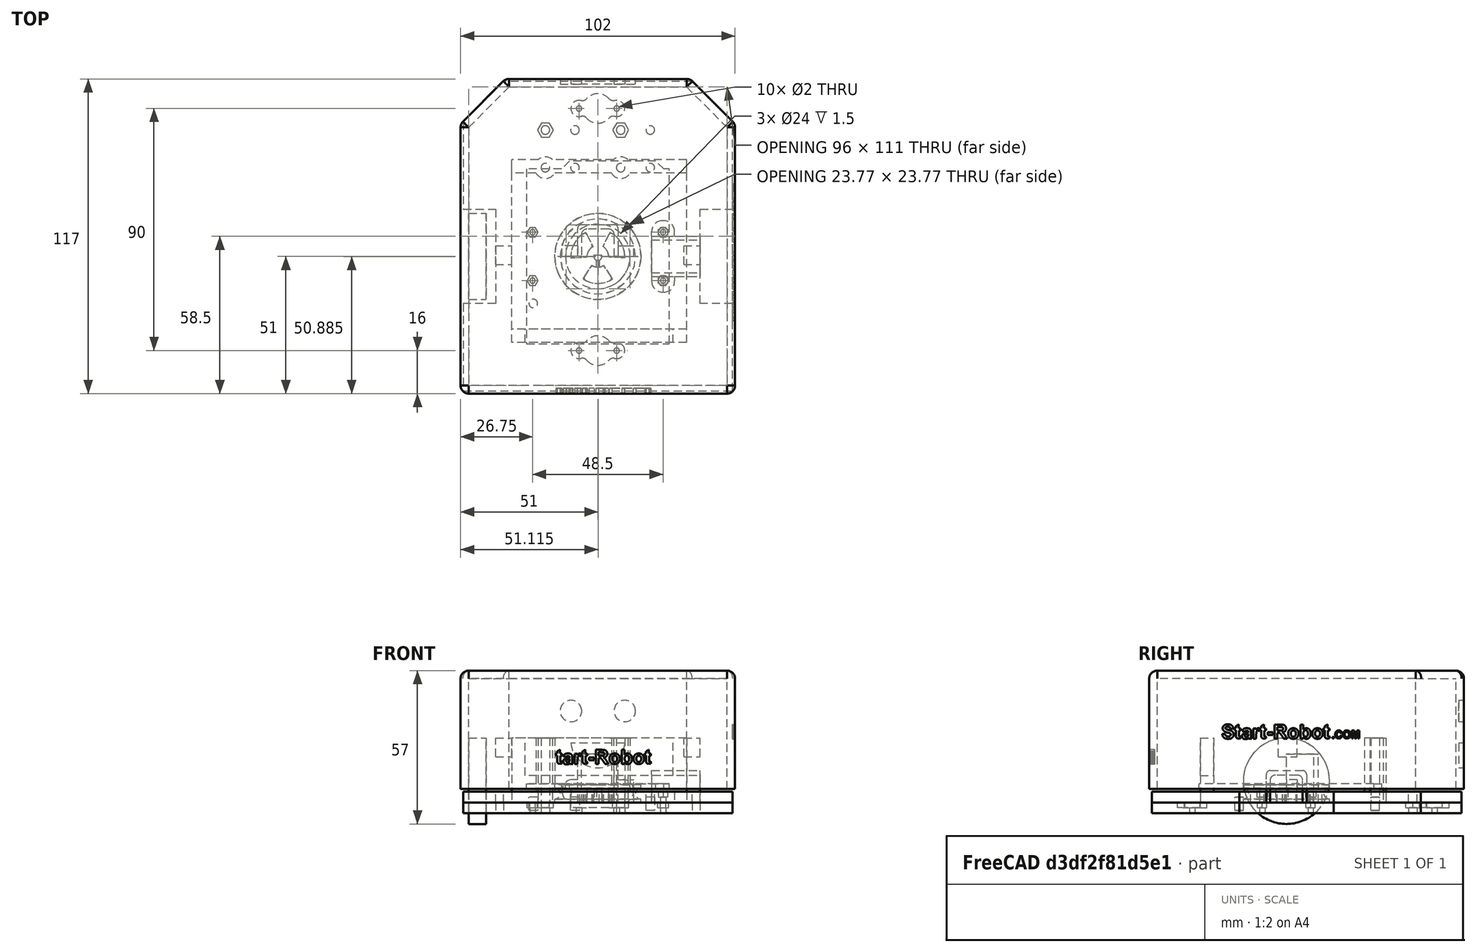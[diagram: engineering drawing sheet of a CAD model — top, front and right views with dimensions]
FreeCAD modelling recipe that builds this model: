
FCSTD DOCUMENT  (FreeCAD 0.14R3700 (Git))
Label: piezasStartCar
License: CC-BY 3.0
LicenseURL: http://creativecommons.org/licenses/by/3.0/
objects: Part::Cut×37, Part::Cylinder×23, Part::Extrusion×16, Part::Feature×15, Sketcher::SketchObject×13, Part::Prism×8, PartDesign::Pocket×7, PartDesign::Pad×6, Part::Box×6, Part::MultiFuse×4, PartDesign::Fillet×3, Mesh::Feature×1, Part::Thickness×1, Part::Torus×1, PartDesign::PolarPattern×1, Part::Fillet×1
note: 155 computed .brp shape members not serialized (recipe doc carries the construction recipe); baked Part::Feature solids carry a one-line shape summary decoded from their .brp

FEATURE [Sketcher::SketchObject] Sketch
  sketch-geometry (14):
    g0: LineSegment StartX=-35 StartY=65 StartZ=0 EndX=35 EndY=65 EndZ=0
    g1: LineSegment StartX=35 StartY=65 StartZ=0 EndX=50 EndY=50 EndZ=0
    g2: LineSegment StartX=50 StartY=50 StartZ=0 EndX=50 EndY=17.5 EndZ=0
    g3: LineSegment StartX=50 StartY=17.5 StartZ=0 EndX=38 EndY=17.5 EndZ=0
    g4: LineSegment StartX=38 StartY=17.5 StartZ=0 EndX=38 EndY=-17.5 EndZ=0
    g5: LineSegment StartX=38 StartY=-17.5 StartZ=0 EndX=50 EndY=-17.5 EndZ=0
    g6: LineSegment StartX=50 StartY=-17.5 StartZ=0 EndX=50 EndY=-50 EndZ=0
    g7: LineSegment StartX=50 StartY=-50 StartZ=0 EndX=-50 EndY=-50 EndZ=0
    g8: LineSegment StartX=-50 StartY=-50 StartZ=0 EndX=-50 EndY=-17.5 EndZ=0
    g9: LineSegment StartX=-50 StartY=-17.5 StartZ=0 EndX=-38 EndY=-17.5 EndZ=0
    g10: LineSegment StartX=-38 StartY=-17.5 StartZ=0 EndX=-38 EndY=17.5 EndZ=0
    g11: LineSegment StartX=-38 StartY=17.5 StartZ=0 EndX=-50 EndY=17.5 EndZ=0
    g12: LineSegment StartX=-50 StartY=17.5 StartZ=0 EndX=-50 EndY=50 EndZ=0
    g13: LineSegment StartX=-50 StartY=50 StartZ=0 EndX=-35 EndY=65 EndZ=0
  constraints (42):
    c: Horizontal(g0)
    c: Coincident(g0,g1)
    c: Coincident(g1,g2)
    c: Vertical(g2)
    c: Coincident(g2,g3)
    c: Coincident(g3,g4)
    c: Coincident(g4,g5)
    c: Coincident(g5,g6)
    c: Vertical(g6)
    c: Coincident(g6,g7)
    c: Horizontal(g7)
    c: Coincident(g7,g8)
    c: Vertical(g8)
    c: Coincident(g8,g9)
    c: Horizontal(g9)
    c: Coincident(g9,g10)
    c: Vertical(g10)
    c: Coincident(g10,g11)
    c: Horizontal(g11)
    c: Coincident(g11,g12)
    c: Coincident(g12,g13)
    c: Coincident(g13,g0)
    c: Equal(g12,g2)
    c: Vertical(g12)
    c: Equal(g10,g4)
    c: Vertical(g4)
    c: Equal(g6,g8)
    c: Equal(g11,g9)
    c: Equal(g3,g5)
    c: Horizontal(g3)
    c: Horizontal(g5)
    c: Symmetric(g0,g0,g-2)
    c: Symmetric(g6,g7,g-2)
    c: DistanceX(g7) = -100
    c: DistanceX(g3) = -12
    c: DistanceX(g11) = -12
    c: DistanceY(g10) = 35
    c: DistanceY(g6) = -32.5
    c: DistanceY(g2) = -32.5
    c: DistanceX(g0) = 70
    c: Angle(g12,g13) = 2.35619
    c: Symmetric(g3,g4,g-1)
FEATURE [PartDesign::Pad] Pad  label="Base"
  Length = 4
  Length2 = 100
  Sketch = -> Sketch
  Type = 0
FEATURE [Sketcher::SketchObject] Sketch001
  Placement = pos=(0,0,5) rot=(0,0,1;0rad)
  sketch-geometry (9):
    g0: LineSegment StartX=-26.5 StartY=32.5 StartZ=0 EndX=-26.5 EndY=-32.5 EndZ=0
    g1: LineSegment StartX=-26.5 StartY=-32.5 StartZ=0 EndX=26.5 EndY=-32.5 EndZ=0
    g2: LineSegment StartX=26.5 StartY=-32.5 StartZ=0 EndX=26.5 EndY=32.5 EndZ=0
    g3: LineSegment StartX=26.5 StartY=32.5 StartZ=0 EndX=24.5 EndY=32.5 EndZ=0
    g4: LineSegment StartX=24.5 StartY=32.5 StartZ=0 EndX=21.5 EndY=35.5 EndZ=0
    g5: LineSegment StartX=21.5 StartY=35.5 StartZ=0 EndX=-10.5 EndY=35.5 EndZ=0
    g6: LineSegment StartX=-10.5 StartY=35.5 StartZ=0 EndX=-13.5 EndY=32.5 EndZ=0
    g7: LineSegment StartX=-13.5 StartY=32.5 StartZ=0 EndX=-26.5 EndY=32.5 EndZ=0
    g8: LineSegment [constr] StartX=-10.5 StartY=35.5 StartZ=0 EndX=-10.5 EndY=-32.5 EndZ=0
  constraints (27):
    c: Vertical(g0)
    c: Coincident(g0,g1)
    c: Horizontal(g1)
    c: Coincident(g1,g2)
    c: Vertical(g2)
    c: Coincident(g2,g3)
    c: Coincident(g3,g4)
    c: Coincident(g4,g5)
    c: Horizontal(g5)
    c: Coincident(g5,g6)
    c: Coincident(g6,g7)
    c: Coincident(g7,g0)
    c: Horizontal(g7)
    c: Equal(g0,g2)
    c: DistanceY(g2) = 65
    c: Coincident(g8,g5)
    c: PointOnObject(g8,g1)
    c: Vertical(g8)
    c: DistanceY(g8) = -68
    c: Horizontal(g3)
    c: DistanceX(g1) = 53
    c: DistanceX(g5) = -32
    c: DistanceX(g3) = -2
    c: DistanceX(g7) = -13
    c: Angle(g6,g5) = 2.35619
    c: Symmetric(g0,g1,g-2)
    c: Symmetric(g0,g0,g-1)
FEATURE [PartDesign::Pad] Pad001
  Length = 2
  Length2 = 100
  Placement = pos=(0,0,5) rot=(0,0,1;0rad)
  Sketch = -> Sketch001
  Type = 0
FEATURE [Sketcher::SketchObject] Sketch002
  ExternalGeometry = -> [Pad001]
  Placement = pos=(0,0,7) rot=(0,0,1;0rad)
  Support = -> Pad001 [Face10]
  sketch-geometry (3):
    g0: Circle CenterX=-24 CenterY=-17.5 CenterZ=0 NormalX=0 NormalY=0 NormalZ=1 Radius=1.6
    g1: Circle CenterX=-8.5 CenterY=33 CenterZ=0 NormalX=0 NormalY=0 NormalZ=1 Radius=1.6
    g2: Circle CenterX=19.5 CenterY=33 CenterZ=0 NormalX=0 NormalY=0 NormalZ=1 Radius=1.6
  constraints (9):
    c: Radius(g0) = 1.6
    c: DistanceY(g0,g-3) = -15
    c: DistanceX(g0,g-3) = 50.5
    c: Equal(g1,g2)
    c: Equal(g2,g0)
    c: DistanceX(g1,g-4) = 35
    c: DistanceY(g1,g-4) = -65.5
    c: DistanceY(g2,g-4) = -65.5
    c: DistanceX(g2,g-4) = 7
FEATURE [PartDesign::Pocket] Pocket  label="Arduino"
  Length = 5
  Placement = pos=(0,0,5) rot=(0,0,1;0rad)
  Sketch = -> Sketch002
  Type = 0
FEATURE [Sketcher::SketchObject] Sketch003
  sketch-geometry (12):
    g0: LineSegment StartX=-6.075 StartY=0 StartZ=0 EndX=-7.5 EndY=0 EndZ=0
    g1: LineSegment StartX=-7.5 StartY=0 StartZ=0 EndX=-7.5 EndY=10.3588 EndZ=0
    g2: LineSegment StartX=-6 StartY=11.8588 StartZ=0 EndX=6 EndY=11.8588 EndZ=0
    g3: LineSegment StartX=7.5 StartY=10.3588 StartZ=0 EndX=7.5 EndY=0 EndZ=0
    g4: LineSegment StartX=7.5 StartY=0 StartZ=0 EndX=6.075 EndY=0 EndZ=0
    g5: LineSegment StartX=6.075 StartY=0 StartZ=0 EndX=6.075 EndY=8.15 EndZ=0
    g6: LineSegment StartX=4.075 StartY=10.15 StartZ=0 EndX=-4.075 EndY=10.15 EndZ=0
    g7: LineSegment StartX=-6.075 StartY=8.15 StartZ=0 EndX=-6.075 EndY=0 EndZ=0
    g8: ArcOfCircle CenterX=6 CenterY=10.3588 CenterZ=0 NormalX=0 NormalY=0 NormalZ=1 Radius=1.5 StartAngle=0 EndAngle=1.5708
    g9: ArcOfCircle CenterX=-6 CenterY=10.3588 CenterZ=0 NormalX=0 NormalY=0 NormalZ=1 Radius=1.5 StartAngle=1.5708 EndAngle=3.14159
    g10: ArcOfCircle CenterX=4.075 CenterY=8.15 CenterZ=0 NormalX=0 NormalY=0 NormalZ=1 Radius=2 StartAngle=0 EndAngle=1.5708
    g11: ArcOfCircle CenterX=-4.075 CenterY=8.15 CenterZ=0 NormalX=0 NormalY=0 NormalZ=1 Radius=2 StartAngle=1.5708 EndAngle=3.14159
  constraints (31):
    c: Horizontal(g0)
    c: Coincident(g0,g1)
    c: Vertical(g1)
    c: Horizontal(g2)
    c: PointOnObject(g3,g-1)
    c: Vertical(g3)
    c: Coincident(g3,g4)
    c: Coincident(g4,g5)
    c: Vertical(g5)
    c: Horizontal(g6)
    c: Coincident(g7,g0)
    c: Vertical(g7)
    c: Horizontal(g4)
    c: Equal(g0,g4)
    c: DistanceX(g0,g3) = 15
    c: DistanceX(g0,g4) = 12.15
    c: Tangent(g2,g8)
    c: Tangent(g3,g8)
    c: Tangent(g2,g9)
    c: Tangent(g1,g9)
    c: Radius(g9) = 1.5
    c: Radius(g8) = 1.5
    c: Tangent(g6,g10)
    c: Tangent(g5,g10)
    c: Tangent(g6,g11)
    c: Tangent(g7,g11)
    c: Radius(g10) = 2
    c: Radius(g11) = 2
    c: DistanceY(g6,g0) = -10.15
    c: DistanceY(g4,g6) = 10.15
    c: Symmetric(g0,g3,g-2)
FEATURE [PartDesign::Pad] Pad002
  Length = 18
  Length2 = 100
  Sketch = -> Sketch003
  Type = 0
FEATURE [Sketcher::SketchObject] Sketch004
  Placement = pos=(7.5,0,0) rot=(0.57735,0.57735,0.57735;2.0944rad)
  Support = -> Pad002 [Face1]
  sketch-geometry (4):
    g0: LineSegment StartX=0 StartY=0 StartZ=0 EndX=4 EndY=0 EndZ=0
    g1: LineSegment StartX=4 StartY=0 StartZ=0 EndX=4 EndY=8.5 EndZ=0
    g2: LineSegment StartX=4 StartY=8.5 StartZ=0 EndX=0 EndY=8.5 EndZ=0
    g3: LineSegment StartX=0 StartY=8.5 StartZ=0 EndX=0 EndY=0 EndZ=0
  constraints (11):
    c: Coincident(g0,g1)
    c: Coincident(g1,g2)
    c: Coincident(g2,g3)
    c: Coincident(g3,g0)
    c: Horizontal(g0)
    c: Horizontal(g2)
    c: Vertical(g1)
    c: Vertical(g3)
    c: Coincident(g0,g-1)
    c: DistanceY(g1) = 8.5
    c: DistanceX(g2) = -4
FEATURE [PartDesign::Pad] Pad003
  Length = 5.8
  Length2 = 100
  Sketch = -> Sketch004
  Type = 0
FEATURE [Sketcher::SketchObject] Sketch005
  Placement = pos=(-7.5,0,0) rot=(0.57735,-0.57735,-0.57735;2.0944rad)
  Support = -> Pad003 [Face10]
  sketch-geometry (4):
    g0: LineSegment StartX=0 StartY=0 StartZ=0 EndX=-4 EndY=0 EndZ=0
    g1: LineSegment StartX=-4 StartY=0 StartZ=0 EndX=-4 EndY=8.5 EndZ=0
    g2: LineSegment StartX=-4 StartY=8.5 StartZ=0 EndX=0 EndY=8.5 EndZ=0
    g3: LineSegment StartX=0 StartY=8.5 StartZ=0 EndX=0 EndY=0 EndZ=0
  constraints (11):
    c: Coincident(g0,g1)
    c: Coincident(g1,g2)
    c: Coincident(g2,g3)
    c: Coincident(g3,g0)
    c: Horizontal(g0)
    c: Horizontal(g2)
    c: Vertical(g1)
    c: Vertical(g3)
    c: Coincident(g0,g-1)
    c: DistanceX(g2) = 4
    c: DistanceY(g1) = 8.5
FEATURE [Part::Prism] Prism  label="Prisma"
  Circumradius = 2
  Height = 2
  Placement = pos=(-9,4,4.25) rot=(1,0,0;1.5708rad)
  Polygon = 6
FEATURE [Part::Prism] Prism002  label="Prisma002"
  Circumradius = 2
  Height = 2
  Placement = pos=(9,4,4.25) rot=(1,0,0;1.5708rad)
  Polygon = 6
FEATURE [Part::Box] Box  label="CNY70"
  Height = 7
  Length = 6
  Placement = pos=(-38,-3,17) rot=(0,0,1;0rad)
  Width = 7
FEATURE [Part::Box] Box001  label="CNY071"
  Height = 7
  Length = 6
  Placement = pos=(32,-3,17) rot=(0,0,1;0rad)
  Width = 7
FEATURE [Part::Cylinder] Cylinder  label="Rueda1"
  Angle = 360
  Height = 6.5
  Radius = 16
FEATURE [Part::Cylinder] Cylinder001  label="Rueda2"
  Angle = 360
  Height = 6.5
  Placement = pos=(-48,0,8) rot=(0,1,0;1.5708rad)
  Radius = 16
FEATURE [Mesh::Feature] baseArduino
  Placement = pos=(0,14,24) rot=(0,0,1;0rad)
FEATURE [Part::Box] Box002  label="Cubo"
  Height = 24
  Length = 65
  Placement = pos=(-33,-18,5) rot=(0,0,1;0rad)
  Width = 5
FEATURE [Part::Box] Box003  label="Cubo001"
  Height = 4
  Length = 65
  Placement = pos=(-33,-13,25) rot=(0,0,1;0rad)
  Width = 63
FEATURE [Part::Box] Box004  label="Cubo002"
  Height = 20
  Length = 65
  Placement = pos=(-33,45,5) rot=(0,0,1;0rad)
  Width = 5
FEATURE [Part::Cylinder] Cylinder003  label="Cilindro001"
  Angle = 360
  Height = 24
  Placement = pos=(19.5,47,5) rot=(0,0,1;0rad)
  Radius = 4
FEATURE [Part::Box] Box005  label="Cubo003"
  Height = 16
  Length = 55
  Placement = pos=(-28,-21,3) rot=(0,0,1;0rad)
  Width = 9
FEATURE [Part::Cylinder] Cylinder004  label="Cilindro002"
  Angle = 360
  Height = 37
  Placement = pos=(-8.5,47,-2) rot=(0,0,1;0rad)
  Radius = 1.6
FEATURE [Part::Cylinder] Cylinder005  label="Cilindro003"
  Angle = 360
  Height = 37
  Placement = pos=(19.5,47,-2) rot=(0,0,1;0rad)
  Radius = 1.6
FEATURE [Part::Cut] Cut006
  Base = -> Pad
  Tool = -> Cylinder004
FEATURE [Part::Cut] Cut008  label="Base001"
  Base = -> Cut006
  Tool = -> Cylinder005
FEATURE [Sketcher::SketchObject] Sketch010
  Placement = pos=(0,0,5) rot=(0,0,1;0rad)
  sketch-geometry (6):
    g0: LineSegment StartX=-33 StartY=63 StartZ=0 EndX=33 EndY=63 EndZ=0
    g1: LineSegment StartX=33 StartY=63 StartZ=0 EndX=48 EndY=48 EndZ=0
    g2: LineSegment StartX=48 StartY=-48 StartZ=0 EndX=-48 EndY=-48 EndZ=0
    g3: LineSegment StartX=-48 StartY=48 StartZ=0 EndX=-33 EndY=63 EndZ=0
    g4: LineSegment StartX=-48 StartY=48 StartZ=0 EndX=-48 EndY=-48 EndZ=0
    g5: LineSegment StartX=48 StartY=48 StartZ=0 EndX=48 EndY=-48 EndZ=0
  constraints (18):
    c: Horizontal(g0)
    c: Coincident(g0,g1)
    c: Horizontal(g2)
    c: Coincident(g3,g0)
    c: Symmetric(g0,g0,g-2)
    c: DistanceX(g2) = -96
    c: DistanceX(g0) = 66
    c: Coincident(g4,g3)
    c: Coincident(g4,g2)
    c: Vertical(g4)
    c: Coincident(g5,g1)
    c: Coincident(g5,g2)
    c: Vertical(g5)
    c: Equal(g5,g4)
    c: DistanceY(g5) = -96
    c: Symmetric(g1,g2,g-1)
    c: Angle(g4,g3) = 2.35619
    c: Angle(g1,g5) = 2.35619
FEATURE [PartDesign::Pad] Pad008  label="Base005"
  Length = 41
  Length2 = 100
  Placement = pos=(0,0,5) rot=(0,0,1;0rad)
  Sketch = -> Sketch010
  Type = 0
FEATURE [Part::Feature] path001
  shape: bbox 2.248 x 5.23 x 2e-07 mm, 0 faces, 0 solids (baked)
FEATURE [Part::Feature] path002
  shape: bbox 3.533 x 4.091 x 2e-07 mm, 0 faces, 0 solids (baked)
FEATURE [Part::Feature] path003
  shape: bbox 1.357 x 1.203 x 2e-07 mm, 0 faces, 0 solids (baked)
FEATURE [Part::Feature] path004
  shape: bbox 2.463 x 3.887 x 2e-07 mm, 0 faces, 0 solids (baked)
FEATURE [Part::Feature] path005
  shape: bbox 2.248 x 5.23 x 2e-07 mm, 0 faces, 0 solids (baked)
FEATURE [Part::Feature] path006
  shape: bbox 1.976 x 1.006 x 2e-07 mm, 0 faces, 0 solids (baked)
FEATURE [Part::Feature] path007
  shape: bbox 4.718 x 5.247 x 2e-07 mm, 0 faces, 0 solids (baked)
FEATURE [Part::Feature] path008
  shape: bbox 2.14 x 1.332 x 2e-07 mm, 0 faces, 0 solids (baked)
FEATURE [Part::Feature] path009
  shape: bbox 3.923 x 3.973 x 2e-07 mm, 0 faces, 0 solids (baked)
FEATURE [Part::Feature] path010
  shape: bbox 1.858 x 2.334 x 2e-07 mm, 0 faces, 0 solids (baked)
FEATURE [Part::Feature] path011
  shape: bbox 3.712 x 5.333 x 2e-07 mm, 0 faces, 0 solids (baked)
FEATURE [Part::Feature] path012
  shape: bbox 1.682 x 2.409 x 2e-07 mm, 0 faces, 0 solids (baked)
FEATURE [Part::Feature] path013
  shape: bbox 3.923 x 3.973 x 2e-07 mm, 0 faces, 0 solids (baked)
FEATURE [Part::Feature] path014
  shape: bbox 1.858 x 2.334 x 2e-07 mm, 0 faces, 0 solids (baked)
FEATURE [Part::Feature] path015
  shape: bbox 2.248 x 5.23 x 2e-07 mm, 0 faces, 0 solids (baked)
FEATURE [Part::Extrusion] Extrude001
  Base = -> path001
  Dir = (0,0,2)
  Solid = true
FEATURE [Part::Extrusion] Extrude002
  Base = -> path002
  Dir = (0,0,2)
  Solid = true
FEATURE [Part::Extrusion] Extrude003
  Base = -> path003
  Dir = (0,0,2)
  Solid = true
FEATURE [Part::Extrusion] Extrude004
  Base = -> path004
  Dir = (0,0,2)
  Solid = true
FEATURE [Part::Extrusion] Extrude005
  Base = -> path005
  Dir = (0,0,2)
  Solid = true
FEATURE [Part::Extrusion] Extrude006
  Base = -> path006
  Dir = (0,0,2)
  Solid = true
FEATURE [Part::Extrusion] Extrude007
  Base = -> path007
  Dir = (0,0,2)
  Solid = true
FEATURE [Part::Extrusion] Extrude008
  Base = -> path008
  Dir = (0,0,2)
  Solid = true
FEATURE [Part::Extrusion] Extrude009
  Base = -> path009
  Dir = (0,0,2)
  Solid = true
FEATURE [Part::Extrusion] Extrude010
  Base = -> path010
  Dir = (0,0,2)
  Solid = true
FEATURE [Part::Extrusion] Extrude011
  Base = -> path011
  Dir = (0,0,2)
  Solid = true
FEATURE [Part::Extrusion] Extrude012
  Base = -> path012
  Dir = (0,0,2)
  Solid = true
FEATURE [Part::Extrusion] Extrude013
  Base = -> path013
  Dir = (0,0,2)
  Solid = true
FEATURE [Part::Extrusion] Extrude014
  Base = -> path014
  Dir = (0,0,2)
  Solid = true
FEATURE [Part::Extrusion] Extrude015
  Base = -> path015
  Dir = (0,0,2)
  Solid = true
FEATURE [Part::Cut] Cut011
  Base = -> Extrude002
  Tool = -> Extrude003
FEATURE [Part::Cut] Cut012
  Base = -> Extrude007
  Tool = -> Extrude008
FEATURE [Part::Cut] Cut013
  Base = -> Extrude009
  Tool = -> Extrude010
FEATURE [Part::Cut] Cut014
  Base = -> Extrude011
  Tool = -> Extrude012
FEATURE [Part::Cut] Cut015
  Base = -> Extrude013
  Tool = -> Extrude014
FEATURE [Part::MultiFuse] Fusion002  label="Nombre"
  Placement = pos=(-3,-49,20) rot=(1,0,0;1.5708rad)
  Shapes = -> [Cut014,Extrude001,Extrude004,Extrude005,Extrude006,Extrude015,Cut015,Cut013,Cut011,Cut012]
FEATURE [Part::Thickness] Thickness
  Faces = -> Pad008 [Face7]
  Intersection = false
  Join = 0
  Mode = 0
  SelfIntersection = false
  Value = 3
FEATURE [Sketcher::SketchObject] Sketch011
  Placement = pos=(0,0,4) rot=(0,0,1;0rad)
  Support = -> Cut008 [Face5]
  sketch-geometry (4):
    g0: Circle CenterX=-7 CenterY=55 CenterZ=0 NormalX=0 NormalY=0 NormalZ=1 Radius=1
    g1: Circle CenterX=7 CenterY=55 CenterZ=0 NormalX=0 NormalY=0 NormalZ=1 Radius=1
    g2: Circle CenterX=-7 CenterY=-35 CenterZ=0 NormalX=0 NormalY=0 NormalZ=1 Radius=1
    g3: Circle CenterX=7 CenterY=-35 CenterZ=0 NormalX=0 NormalY=0 NormalZ=1 Radius=1
  constraints (10):
    c: Equal(g0,g1)
    c: Equal(g1,g3)
    c: Equal(g3,g2)
    c: Radius(g0) = 1
    c: DistanceX(g2,g3) = 14
    c: Symmetric(g3,g2,g-2)
    c: DistanceX(g1,g0) = -14
    c: Symmetric(g1,g0,g-2)
    c: DistanceY(g-1,g1) = 55
    c: DistanceY(g-1,g2) = -35
FEATURE [PartDesign::Pocket] Pocket002  label="BaseCoche"
  Length = 5
  Sketch = -> Sketch011
  Type = 0
FEATURE [Part::Cylinder] Cylinder009  label="Cilindro007"
  Angle = 360
  Height = 11
  Placement = pos=(-24.25,9,-3) rot=(0,0,1;0rad)
  Radius = 1
FEATURE [Part::Cylinder] Cylinder010  label="Cilindro008"
  Angle = 360
  Height = 11
  Placement = pos=(-24.25,-9,-3) rot=(0,0,1;0rad)
  Radius = 1
FEATURE [Part::Cylinder] Cylinder011  label="Cilindro009"
  Angle = 360
  Height = 11
  Placement = pos=(24.25,-9,-2) rot=(0,0,1;0rad)
  Radius = 1
FEATURE [Part::Cylinder] Cylinder012  label="Cilindro010"
  Angle = 360
  Height = 11
  Placement = pos=(24.25,9,-3) rot=(0,0,1;0rad)
  Radius = 1
FEATURE [Part::Cut] Cut016
  Base = -> Pocket002
  Tool = -> Cylinder009
FEATURE [Part::Cut] Cut017
  Base = -> Cut016
  Tool = -> Cylinder010
FEATURE [Part::Cut] Cut018
  Base = -> Cut017
  Tool = -> Cylinder011
FEATURE [Part::Cut] Cut019
  Base = -> Cut018
  Placement = pos=(0,0,0) rot=(0,1,0;3.14159rad)
  Tool = -> Cylinder012
FEATURE [Part::Cylinder] Cylinder013  label="Cilindro011"
  Angle = 360
  Height = 24
  Placement = pos=(-8.5,47,5) rot=(0,0,1;0rad)
  Radius = 4
FEATURE [Part::MultiFuse] Fusion
  Shapes = -> [Box002,Box003,Box004,Cylinder003,Cylinder013]
FEATURE [Part::Cut] Cut004
  Base = -> Fusion
  Tool = -> Box005
FEATURE [Part::Cut] Cut005
  Base = -> Cut004
  Tool = -> Cylinder004
FEATURE [Part::Prism] Prism003  label="Prisma003"
  Circumradius = 2
  Height = 4
  Polygon = 6
FEATURE [Part::Cylinder] Cylinder014  label="Cilindro"
  Angle = 360
  Height = 10
  Placement = pos=(0,0,-3) rot=(0,0,1;0rad)
  Radius = 1
FEATURE [Part::Cut] Cut020
  Base = -> Prism003
  Placement = pos=(-24.25,9,-2) rot=(0,0,1;0rad)
  Tool = -> Cylinder014
FEATURE [Part::Cylinder] Cylinder015  label="Cilindro012"
  Angle = 360
  Height = 10
  Placement = pos=(0,0,-3) rot=(0,0,1;0rad)
  Radius = 1
FEATURE [Part::Prism] Prism004  label="Prisma004"
  Circumradius = 2
  Height = 2
  Polygon = 6
FEATURE [Part::Cut] Cut021
  Base = -> Prism004
  Placement = pos=(-24.25,-9,-2) rot=(0,0,1;0rad)
  Tool = -> Cylinder015
FEATURE [Part::Cylinder] Cylinder016  label="Cilindro013"
  Angle = 360
  Height = 10
  Placement = pos=(0,0,-3) rot=(0,0,1;0rad)
  Radius = 1
FEATURE [Part::Prism] Prism005  label="Prisma005"
  Circumradius = 2
  Height = 2
  Polygon = 6
FEATURE [Part::Cut] Cut022
  Base = -> Prism005
  Placement = pos=(24.25,9,-2) rot=(0,0,1;0rad)
  Tool = -> Cylinder016
FEATURE [Part::Cylinder] Cylinder017  label="Cilindro014"
  Angle = 360
  Height = 10
  Placement = pos=(0,0,-3) rot=(0,0,1;0rad)
  Radius = 1
FEATURE [Part::Prism] Prism006  label="Prisma006"
  Circumradius = 2
  Height = 2
  Polygon = 6
FEATURE [Part::Cut] Cut023
  Base = -> Prism006
  Placement = pos=(24.25,-9,-2) rot=(0,0,1;0rad)
  Tool = -> Cylinder017
FEATURE [Part::Cut] Cut024
  Base = -> Cut019
  Tool = -> Cut020
FEATURE [Part::Cut] Cut025
  Base = -> Cut024
  Tool = -> Cut023
FEATURE [Part::Cut] Cut026
  Base = -> Cut025
  Tool = -> Cut022
FEATURE [Part::Cut] Cut027
  Base = -> Cut026
  Tool = -> Cut021
FEATURE [Part::Prism] Prism007  label="Prisma007"
  Circumradius = 3
  Height = 2
  Polygon = 6
FEATURE [Part::Cylinder] Cylinder018  label="Cilindro015"
  Angle = 360
  Height = 10
  Radius = 1.5
FEATURE [Part::Cut] Cut028  label="primas3M01"
  Base = -> Prism007
  Placement = pos=(-19.5,47,-2) rot=(0,0,1;0rad)
  Tool = -> Cylinder018
FEATURE [Part::Prism] Prism008  label="Prisma008"
  Circumradius = 3
  Height = 2
  Polygon = 6
FEATURE [Part::Cylinder] Cylinder019  label="Cilindro016"
  Angle = 360
  Height = 10
  Radius = 1.5
FEATURE [Part::Cut] Cut029  label="primas3M002"
  Base = -> Prism008
  Placement = pos=(8.5,47,-2) rot=(0,0,1;0rad)
  Tool = -> Cylinder019
FEATURE [Part::Cut] Cut034
  Base = -> Cut027
  Tool = -> Cut028
FEATURE [PartDesign::Pad] Pad009
  Length = 5.8
  Length2 = 100
  Sketch = -> Sketch005
  Type = 0
FEATURE [PartDesign::Fillet] Fillet
  Base = -> Pad009 [Edge59,Edge48]
  Radius = 4
FEATURE [PartDesign::Fillet] Fillet001
  Base = -> Fillet [Edge63,Edge56]
  Radius = 4
FEATURE [Sketcher::SketchObject] Sketch006
  Placement = pos=(0,0,0) rot=(1,0,0;1.5708rad)
  Support = -> Fillet001 [Face25]
  sketch-geometry (2):
    g0: Circle CenterX=-9 CenterY=4.25 CenterZ=0 NormalX=0 NormalY=0 NormalZ=1 Radius=1
    g1: Circle CenterX=9 CenterY=4.25 CenterZ=0 NormalX=0 NormalY=0 NormalZ=1 Radius=1
  constraints (5):
    c: Equal(g1,g0)
    c: Radius(g0) = 1
    c: DistanceX(g0,g1) = 18
    c: Symmetric(g1,g0,g-2)
    c: DistanceY(g-1,g0) = 4.25
FEATURE [PartDesign::Pocket] Pocket003
  Length = 5
  Sketch = -> Sketch006
  Type = 0
FEATURE [Part::Cut] Cut040
  Base = -> Pocket003
  Tool = -> Prism
FEATURE [Part::Cut] Cut041  label="marcoMotor001"
  Base = -> Cut040
  Placement = pos=(20,0,0) rot=(0.57735,0.57735,0.57735;2.0944rad)
  Tool = -> Prism002
FEATURE [Part::Cut] Cut007  label="SoporteArduino"
  Base = -> Cut005
  Placement = pos=(0,-14,29) rot=(0,1,0;3.14159rad)
  Tool = -> Cylinder005
FEATURE [Part::Torus] Torus  label="Toro"
  Angle1 = -180
  Angle2 = 180
  Angle3 = 360
  Placement = pos=(0,0,3.25) rot=(0,0,1;0rad)
  Radius1 = 16
  Radius2 = 2
FEATURE [Part::Cut] Cut
  Base = -> Cylinder
  Tool = -> Torus
FEATURE [Part::Cylinder] Cylinder023  label="Cilindro020"
  Angle = 360
  Height = 10
  Placement = pos=(0,0,5) rot=(0,0,1;0rad)
  Radius = 12
FEATURE [Part::Cut] Cut042
  Base = -> Cut
  Tool = -> Cylinder023
FEATURE [Sketcher::SketchObject] Sketch012
  Placement = pos=(0,0,0) rot=(1,0,0;3.14159rad)
  Support = -> Cut042 [Face7]
  sketch-geometry (4):
    g0: ArcOfCircle CenterX=0 CenterY=0 CenterZ=0 NormalX=0 NormalY=0 NormalZ=1 Radius=10 StartAngle=0.987326 EndAngle=2.15427
    g1: ArcOfCircle CenterX=0 CenterY=0 CenterZ=0 NormalX=0 NormalY=0 NormalZ=1 Radius=4 StartAngle=0.987326 EndAngle=2.15427
    g2: LineSegment StartX=-5.50923 StartY=8.34556 StartZ=0 EndX=-2.20369 EndY=3.33822 EndZ=0
    g3: LineSegment StartX=5.50923 StartY=8.34556 StartZ=0 EndX=2.20369 EndY=3.33822 EndZ=0
  constraints (12):
    c: Coincident(g0,g-1)
    c: Radius(g0) = 10
    c: Coincident(g1,g-1)
    c: Radius(g1) = 4
    c: Perpendicular(g2,g0)
    c: Perpendicular(g3,g0)
    c: Coincident(g0,g3)
    c: Coincident(g0,g2)
    c: Coincident(g1,g3)
    c: Coincident(g1,g2)
    c: DistanceY(g-1,g1) = 3.33822
    c: DistanceY(g-1,g0) = 8.34556
FEATURE [PartDesign::Pocket] Pocket004
  Length = 5
  Sketch = -> Sketch012
  Type = 0
FEATURE [PartDesign::PolarPattern] PolarPattern
  Angle = 360
  Axis = -> Sketch012 [N_Axis]
  Occurrences = 3
  Originals = -> [Pocket004]
FEATURE [Sketcher::SketchObject] Sketch013
  Placement = pos=(0,0,5) rot=(0,0,1;0rad)
  Support = -> PolarPattern [Face6]
  sketch-geometry (2):
    g0: ArcOfCircle CenterX=0 CenterY=0 CenterZ=0 NormalX=0 NormalY=0 NormalZ=1 Radius=1.5 StartAngle=2.80176 EndAngle=6.62302
    g1: LineSegment StartX=-1.41421 StartY=0.5 StartZ=0 EndX=1.41421 EndY=0.5 EndZ=0
  constraints (6):
    c: Coincident(g0,g-1)
    c: Radius(g0) = 1.5
    c: Coincident(g0,g1)
    c: Coincident(g0,g1)
    c: DistanceY(g-1,g0) = 0.5
    c: Horizontal(g1)
FEATURE [Part::Cut] Cut043
  Base = -> Cut034
  Tool = -> Cut029
FEATURE [Part::Cylinder] Cylinder024  label="Cilindro021"
  Angle = 360
  Height = 3
  Radius = 3
FEATURE [Part::Cylinder] Cylinder025  label="Cilindro022"
  Angle = 360
  Height = 3
  Placement = pos=(14,0,0) rot=(0,0,1;0rad)
  Radius = 3
FEATURE [Part::Cylinder] Cylinder026  label="Cilindro023"
  Angle = 360
  Height = 3
  Placement = pos=(7,0,0) rot=(0,0,1;0rad)
  Radius = 5.5
FEATURE [Part::MultiFuse] Fusion003
  Shapes = -> [Cylinder024,Cylinder025,Cylinder026]
FEATURE [Part::Fillet] Fillet005
  Base = -> Fusion003
  Edges = 4 edges r=2: [Edge1,Edge3,Edge6,Edge9]
FEATURE [Part::Cylinder] Cylinder027  label="Cilindro024"
  Angle = 360
  Height = 10
  Placement = pos=(0,0,-4) rot=(0,0,1;0rad)
  Radius = 1
FEATURE [Part::Cylinder] Cylinder028  label="Cilindro025"
  Angle = 360
  Height = 10
  Placement = pos=(14,0,-4) rot=(0,0,1;0rad)
  Radius = 1
FEATURE [Part::Cut] Cut044
  Base = -> Fillet005
  Tool = -> Cylinder027
FEATURE [Part::Cut] Cut045
  Base = -> Cut044
  Placement = pos=(-7,55,-2) rot=(0,0,1;0rad)
  Tool = -> Cylinder028
FEATURE [Part::Cylinder] Cylinder029  label="Cilindro026"
  Angle = 360
  Height = 10
  Placement = pos=(14,0,-4) rot=(0,0,1;0rad)
  Radius = 1
FEATURE [Part::Cut] Cut047
  Base = -> Fillet005
  Tool = -> Cylinder027
FEATURE [Part::Cut] Cut046
  Base = -> Cut047
  Placement = pos=(-7,-35,-2) rot=(0,0,1;0rad)
  Tool = -> Cylinder029
FEATURE [Part::Cut] Cut048
  Base = -> Cut043
  Tool = -> Cut045
FEATURE [Part::Cut] Cut049  label="baseCubetto3D"
  Base = -> Cut048
  Tool = -> Cut046
FEATURE [PartDesign::Pocket] Pocket007
  Length = 5
  Sketch = -> Sketch013
  Type = 0
FEATURE [Sketcher::SketchObject] Sketch014
  Placement = pos=(0,0,5) rot=(0,0,1;0rad)
  Support = -> Pocket007 [Face6]
  sketch-geometry (4):
    g0: LineSegment StartX=-0.5 StartY=-1 StartZ=0 EndX=0.5 EndY=-1 EndZ=0
    g1: LineSegment StartX=0.5 StartY=-1 StartZ=0 EndX=0.5 EndY=-4 EndZ=0
    g2: LineSegment StartX=0.5 StartY=-4 StartZ=0 EndX=-0.5 EndY=-4 EndZ=0
    g3: LineSegment StartX=-0.5 StartY=-4 StartZ=0 EndX=-0.5 EndY=-1 EndZ=0
  constraints (14):
    c: Coincident(g0,g1)
    c: Coincident(g1,g2)
    c: Coincident(g2,g3)
    c: Coincident(g3,g0)
    c: Horizontal(g0)
    c: Vertical(g1)
    c: Vertical(g3)
    c: Equal(g0,g2)
    c: Equal(g1,g3)
    c: Symmetric(g1,g2,g-2)
    c: DistanceY(g-1,g0) = -1
    c: DistanceY(g1) = -3
    c: DistanceY(g-1,g2) = -4
    c: DistanceX(g0) = 1
FEATURE [PartDesign::Pocket] Pocket008
  Length = 5
  Sketch = -> Sketch014
  Type = 0
FEATURE [PartDesign::Fillet] Fillet006  label="Rueda"
  Base = -> Pocket008 [Edge62,Edge63,Edge61,Edge60,Edge66,Edge64,Edge67,Edge65,Edge54,Edge55,Edge56,Edge53]
  Radius = 1
FEATURE [Sketcher::SketchObject] Sketch015
  ExternalGeometry = -> [Thickness]
  Placement = pos=(0,66,0) rot=(0,0.707107,0.707107;3.14159rad)
  Support = -> Thickness [Face13]
  sketch-geometry (4):
    g0: Circle CenterX=-10 CenterY=34 CenterZ=0 NormalX=0 NormalY=0 NormalZ=1 Radius=4
    g1: Circle CenterX=10 CenterY=34 CenterZ=0 NormalX=0 NormalY=0 NormalZ=1 Radius=4
    g2: LineSegment StartX=-10 StartY=22 StartZ=0 EndX=10 EndY=22 EndZ=0
    g3: ArcOfCircle CenterX=0 CenterY=22.924 CenterZ=0 NormalX=0 NormalY=0 NormalZ=1 Radius=10.0426 StartAngle=3.23373 EndAngle=6.19104
  constraints (12):
    c: Equal(g1,g0)
    c: Symmetric(g1,g0,g-2)
    c: Radius(g1) = 4
    c: DistanceX(g0,g1) = 20
    c: Horizontal(g2)
    c: Symmetric(g2,g2,g-2)
    c: DistanceX(g2) = 20
    c: Coincident(g3,g2)
    c: Coincident(g3,g2)
    c: DistanceY(g2,g1) = 12
    c: DistanceY(g1,g-3) = 12
    c: Radius(g3) = 10.0426
FEATURE [PartDesign::Pocket] Pocket009
  Length = 2
  Sketch = -> Sketch015
  Type = 0
FEATURE [Part::MultiFuse] Fusion004
FEATURE [Part::Extrusion] Extrude  label="texto2"
  Base = -> Fusion004
  Dir = (0,0,2)
  Placement = pos=(50,-6,26) rot=(0.57735,0.57735,0.57735;2.0944rad)
  Solid = true
FEATURE [Part::Cut] Cut050
  Base = -> Pocket009
  Tool = -> Extrude
